# Revit family: Sanitary_Urinals_Johnson-Suisse_Life_Electronic_Urinal_Back_Entry
name_source: partatom
category: Plumbing Fixtures
revit_build: Autodesk Revit 2015 (Build: 20140606_1530(x64)
units: mm (PartAtom-declared; Revit-internal decimal feet)

## types (1)
- Life Electronic Urinal Back Entry
    BIMobject category = Urinals
    Brand url = http://www.johnsonsuisse.com.au
    Design country = Spain
    EAN code = https://9325304001616
    Edition number = 1
    IFC Classification = Sanitary Terminal
    Manufacturer country = China
    Manufacturer name = Johnson Suisse
    Material main = Vitreous china
    NBS Reference Code = 35-93-82
    NBS Reference Description = Wall-Hung Urinals
    Nominal height = 660 mm  [stored 2.16535 ft]
    Nominal width = 360 mm  [stored 1.1811 ft]
    OmniClass Code = 23-31 21 00
    OmniClass Description = Urinals
    Product Guid = 5929f6ce-4816-458d-883e-bd7ab3125420
    Product SKU = J6010
    Product data url = https://bimobject.com
    Product family = Life
    Product group = Urinals
    Product url = https://johnsonsuisse.com.au
    QR code = http://bimobject.com
    Technical description = https://johnsonsuisse.com.au
    Type = life_electronic_urinal_back_entry : Default
    UNSPSC Code = 301815
    Uniclass 1.4 Code = L7217
    Uniclass 1.4 Description = Urinals
    Uniclass 2.0 Code = PR-35-93-82
    Uniclass 2.0 Description = Wall-Hung Urinals
    Uniclass 2015 Code = Pr_40_20_93_82
    Uniclass 2015 Name = Wall-hung urinals
    Weight Net (Kg) = 24

note: [stored X ft] marks values corroborated as IEEE doubles in the binary element streams (Revit-internal decimal feet)

## geometry (parser evidence)
native form markers: Sweep x6
no freeform markers — native parametric forms only
